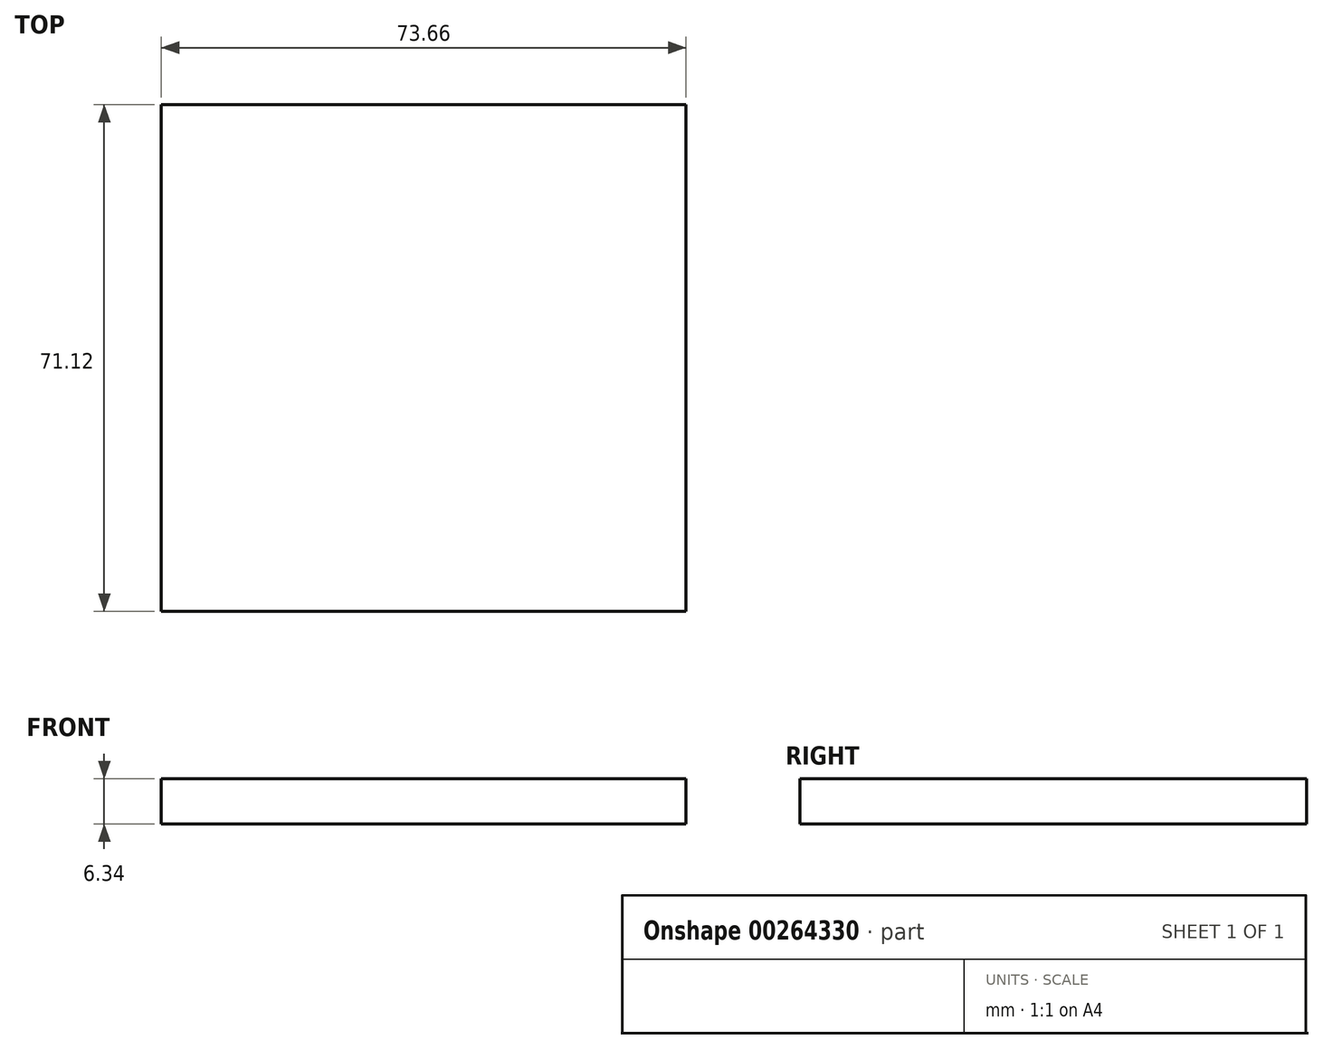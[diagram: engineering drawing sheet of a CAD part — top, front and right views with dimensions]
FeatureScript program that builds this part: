
annotation { "Feature Type Name" : "Feature", "Feature Type Description" : "" }
export const myFeature = defineFeature(function(context is Context, id is Id, definition is map)
    precondition{}
    {
        {
            var Q0;
            Q0=qCreatedBy(makeId("Front.planeOp"),FACE);
            var sketch = newSketch(context, id + "F0", { "sketchPlane" : qUnion([Q0])});
            skLineSegment(sketch, "E0.bottom", {"start": v(36.83, 3.18) * mm, "end": v(-36.83, 3.18) * mm});
            skLineSegment(sketch, "E0.top", {"start": v(36.83, -3.18) * mm, "end": v(-36.83, -3.18) * mm});
            skLineSegment(sketch, "E0.left", {"start": v(36.83, 3.18) * mm, "end": v(36.83, -3.18) * mm});
            skLineSegment(sketch, "E0.right", {"start": v(-36.83, 3.18) * mm, "end": v(-36.83, -3.18) * mm});
            skPoint(sketch, "E0.middle", {"position": v(0, 0) * mm});
            skSolve(sketch);
        }
        {
            var Q0;
            Q0=makeQuery(id+"F0.imprint","IMPRINT",FACE,{"disambiguationData":[TD([[makeQuery(id+"F0.imprint","IMPRINT",EDGE,{"derivedFrom":sQuery(id+"F0.wireOp",EDGE,"E0.bottom")}),1.0]])]});
            extrude(context, id + "F1", {"entities" : qUnion([Q0]), "depth" : 71.12 * mm});
        }
    });
